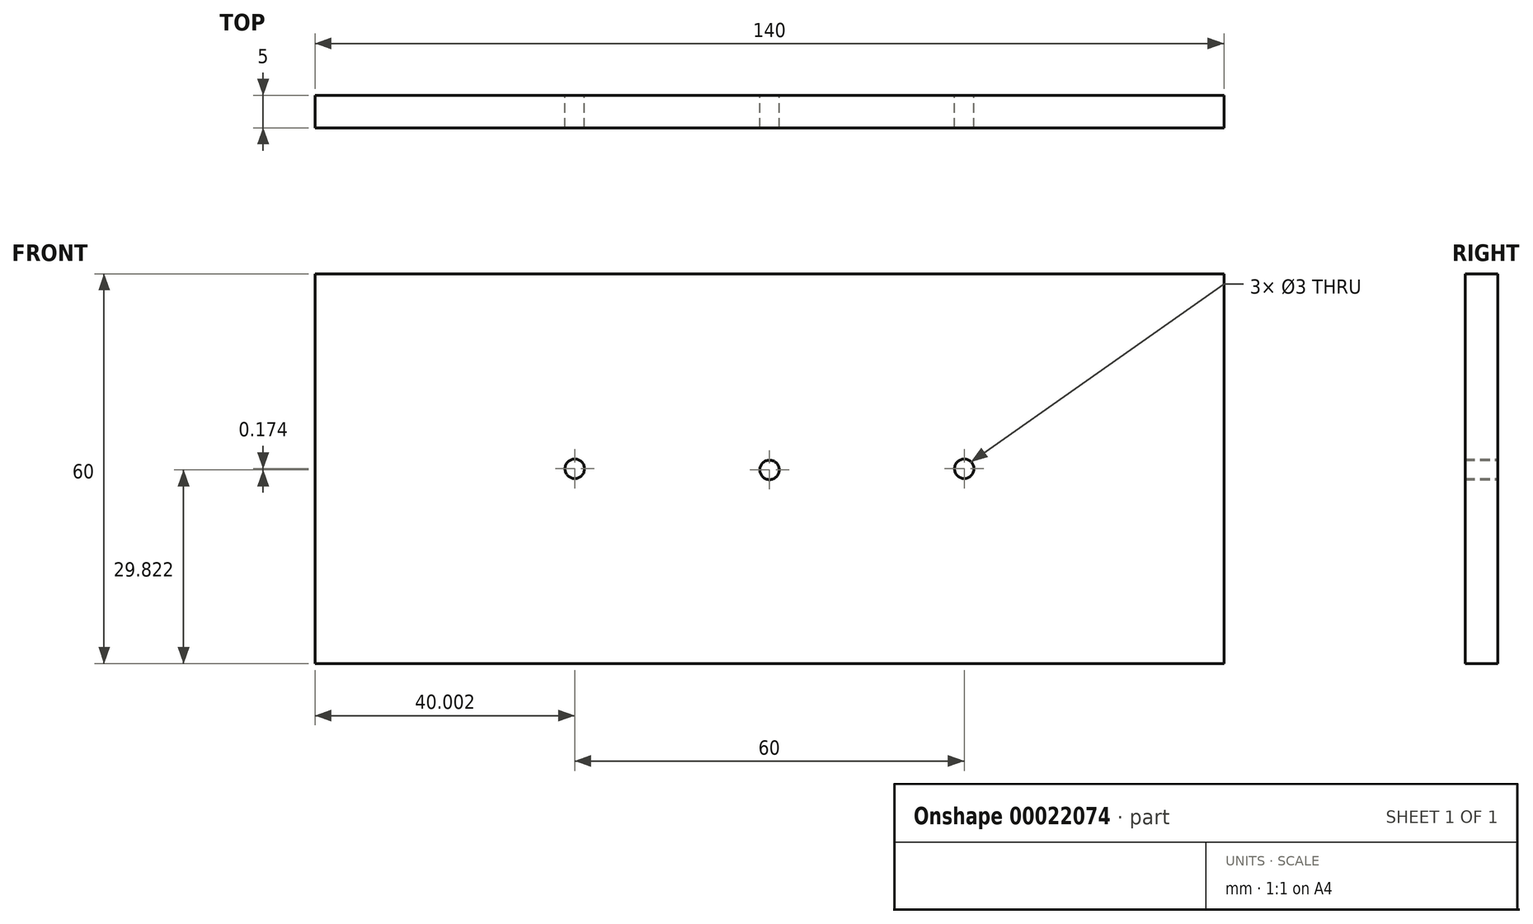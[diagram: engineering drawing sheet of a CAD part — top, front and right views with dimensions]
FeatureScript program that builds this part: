
annotation { "Feature Type Name" : "Feature", "Feature Type Description" : "" }
export const myFeature = defineFeature(function(context is Context, id is Id, definition is map)
    precondition{}
    {
        {
            var Q0;
            Q0=qCreatedBy(makeId("Front.planeOp"),FACE);
            var sketch = newSketch(context, id + "F0", { "sketchPlane" : qUnion([Q0])});
            skCircle(sketch, "E0", {"center": v(9.7, -14.34) * mm, "radius": 1.5 * mm});
            skCircle(sketch, "E1", {"center": v(69.7, -14.34) * mm, "radius": 1.5 * mm});
            skLineSegment(sketch, "E2", {"start": v(-30.3, 15.66) * mm, "end": v(-30.3, -44.34) * mm});
            skLineSegment(sketch, "E3", {"start": v(-30.3, -44.34) * mm, "end": v(109.7, -44.34) * mm});
            skLineSegment(sketch, "E4", {"start": v(-30.3, 15.66) * mm, "end": v(109.7, 15.66) * mm});
            skLineSegment(sketch, "E5", {"start": v(109.7, -44.34) * mm, "end": v(109.7, 15.66) * mm});
            skCircle(sketch, "E6", {"center": v(39.7, -14.52) * mm, "radius": 1.5 * mm});
            skSolve(sketch);
        }
        {
            var Q0;
            Q0=qSketchRegion(id+"F0",true);
            extrude(context, id + "F1", {"entities" : qUnion([Q0]), "endBound" : BoundingType.SYMMETRIC, "depth" : 5 * mm});
        }
    });
